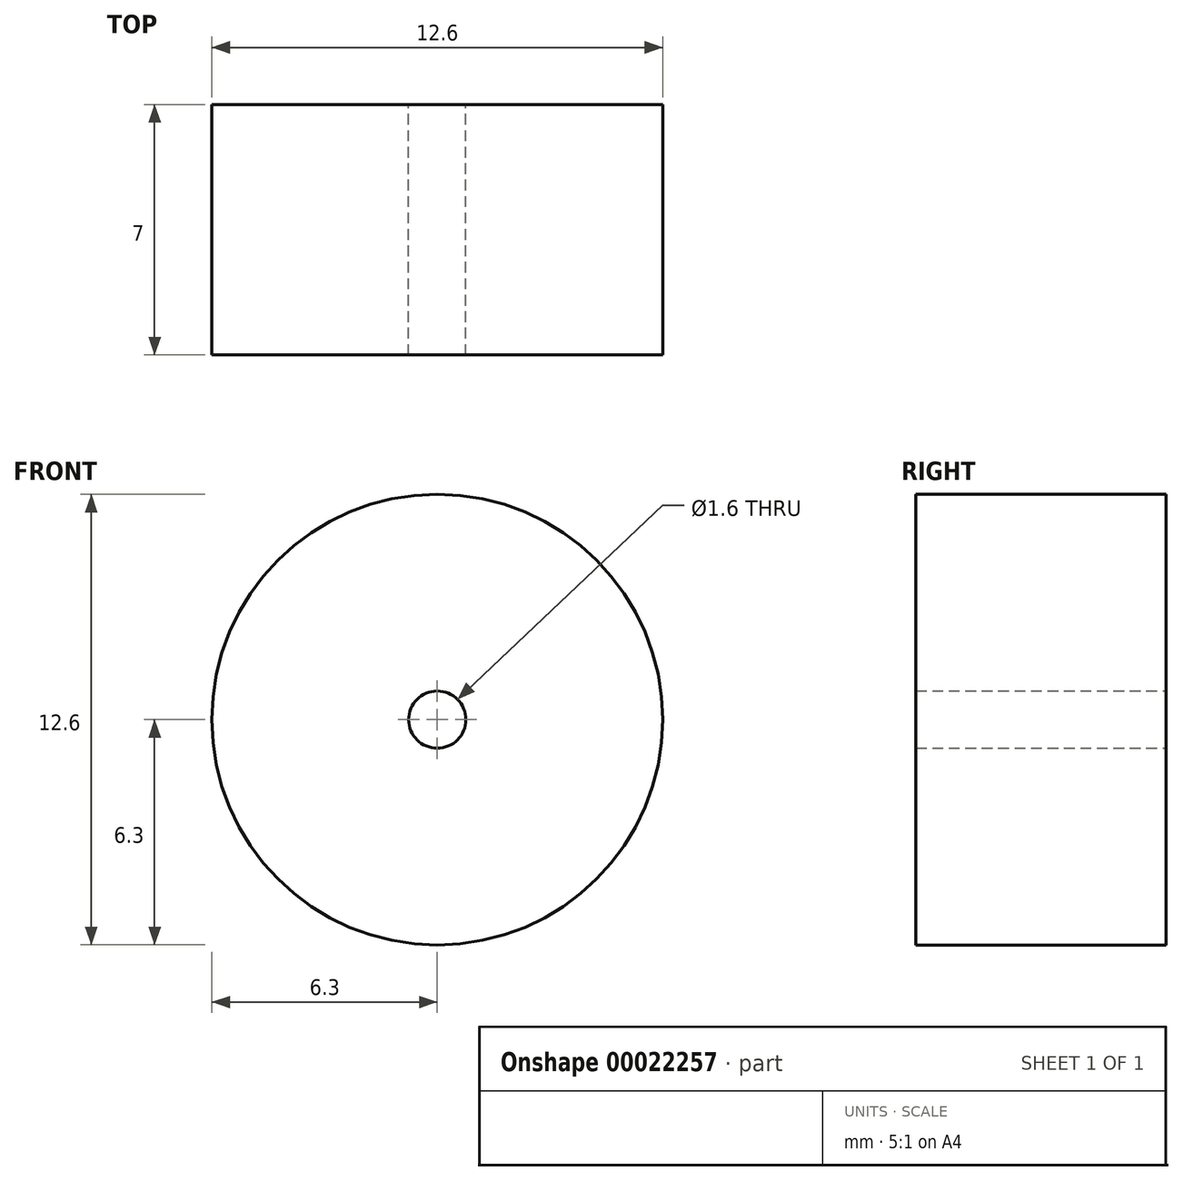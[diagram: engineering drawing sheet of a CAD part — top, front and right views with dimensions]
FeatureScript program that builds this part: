
annotation { "Feature Type Name" : "Feature", "Feature Type Description" : "" }
export const myFeature = defineFeature(function(context is Context, id is Id, definition is map)
    precondition{}
    {
        {
            var Q0;
            Q0=qCreatedBy(makeId("Front.planeOp"),FACE);
            var sketch = newSketch(context, id + "F0", { "sketchPlane" : qUnion([Q0])});
            skCircle(sketch, "E0", {"center": v(0, 0) * mm, "radius": 6.3 * mm});
            skCircle(sketch, "E1", {"center": v(0, 0) * mm, "radius": 0.8 * mm});
            skSolve(sketch);
        }
        {
            var Q0;
            Q0=makeQuery(id+"F0.imprint","IMPRINT",FACE,{"disambiguationData":[TD([[makeQuery(id+"F0.imprint","IMPRINT",EDGE,{"derivedFrom":sQuery(id+"F0.wireOp",EDGE,"E0")}),1.0]])]});
            extrude(context, id + "F1", {"entities" : qUnion([Q0]), "depth" : 7 * mm});
        }
    });
